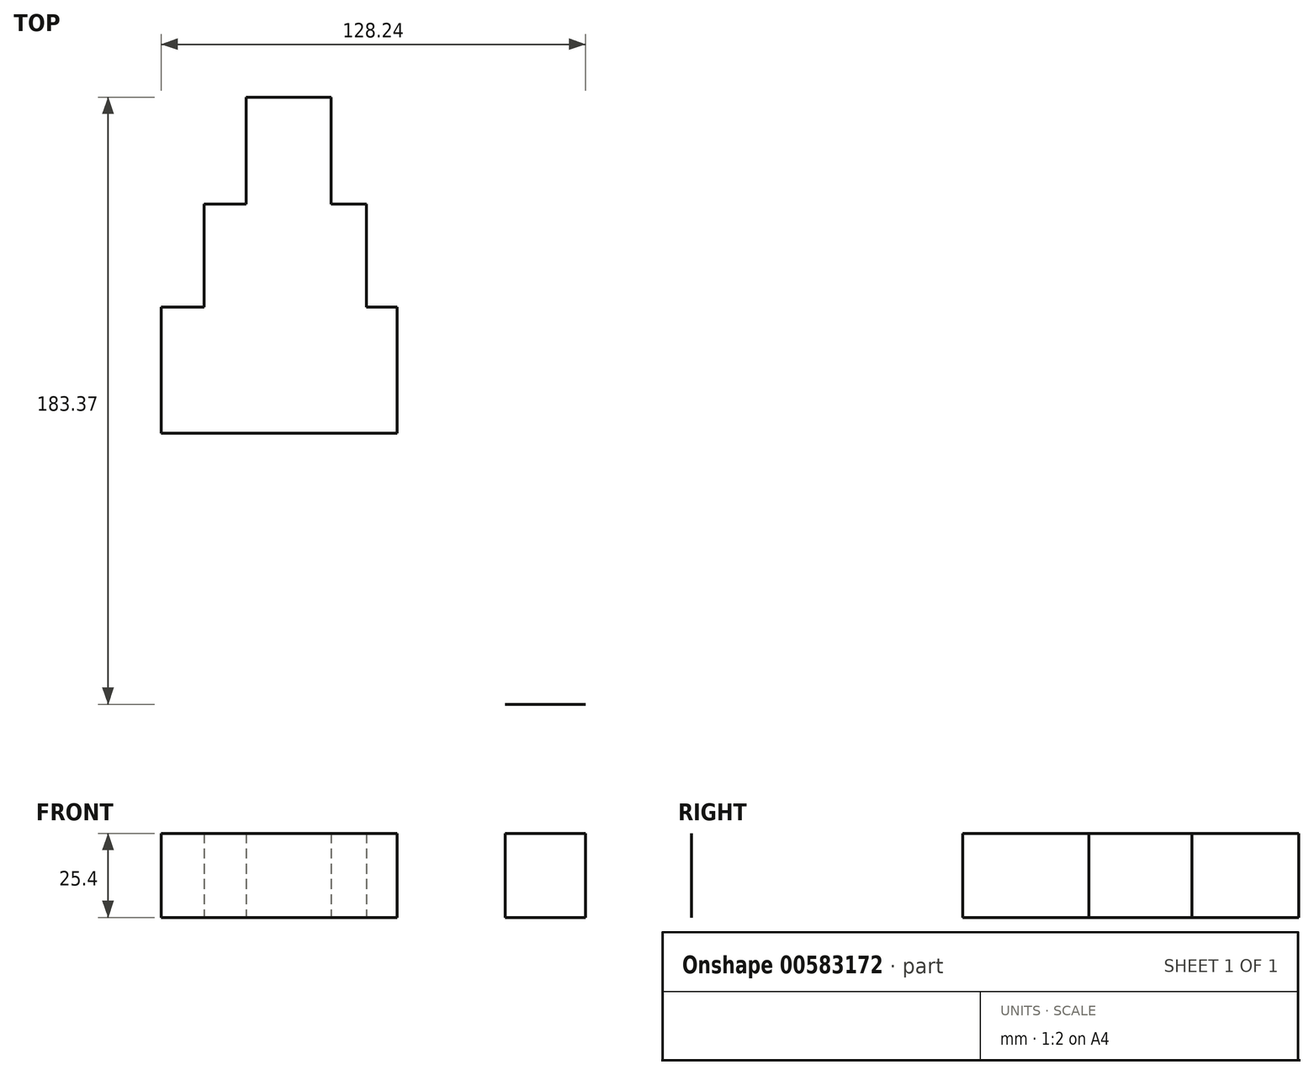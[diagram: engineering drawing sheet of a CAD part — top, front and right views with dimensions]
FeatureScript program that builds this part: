
annotation { "Feature Type Name" : "Feature", "Feature Type Description" : "" }
export const myFeature = defineFeature(function(context is Context, id is Id, definition is map)
    precondition{}
    {
        {
            var Q0;
            Q0=qCreatedBy(makeId("Top.planeOp"),FACE);
            var sketch = newSketch(context, id + "F0", { "sketchPlane" : qUnion([Q0])});
            skLineSegment(sketch, "E0.bottom", {"start": v(-203.2, 189.34) * mm, "end": v(0, 189.34) * mm});
            skLineSegment(sketch, "E0.top", {"start": v(-203.2, -13.86) * mm, "end": v(0, -13.86) * mm});
            skLineSegment(sketch, "E0.left", {"start": v(-203.2, 189.34) * mm, "end": v(-203.2, -13.86) * mm});
            skLineSegment(sketch, "E0.right", {"start": v(0, 189.34) * mm, "end": v(0, -13.86) * mm});
            skText(sketch, "E1", { "text": "A\n", "fontName": "OpenSans-Regular.ttf"});
            skLineSegment(sketch, "E2.bottom", {"start": v(-152.85, 67.96) * mm, "end": v(-81.5, 67.96) * mm});
            skLineSegment(sketch, "E2.top", {"start": v(-152.85, 106.14) * mm, "end": v(-81.5, 106.14) * mm});
            skLineSegment(sketch, "E2.left", {"start": v(-152.85, 67.96) * mm, "end": v(-152.85, 106.14) * mm});
            skLineSegment(sketch, "E2.right", {"start": v(-81.5, 67.96) * mm, "end": v(-81.5, 106.14) * mm});
            skLineSegment(sketch, "E3.bottom", {"start": v(-139.84, 106.14) * mm, "end": v(-90.79, 106.14) * mm});
            skLineSegment(sketch, "E3.top", {"start": v(-139.84, 137.26) * mm, "end": v(-90.79, 137.26) * mm});
            skLineSegment(sketch, "E3.left", {"start": v(-139.84, 106.14) * mm, "end": v(-139.84, 137.26) * mm});
            skLineSegment(sketch, "E3.right", {"start": v(-90.79, 106.14) * mm, "end": v(-90.79, 137.26) * mm});
            skLineSegment(sketch, "E4.bottom", {"start": v(-127.18, 169.5) * mm, "end": v(-101.47, 169.5) * mm});
            skLineSegment(sketch, "E4.top", {"start": v(-127.18, 137.26) * mm, "end": v(-101.47, 137.26) * mm});
            skLineSegment(sketch, "E4.left", {"start": v(-127.18, 169.5) * mm, "end": v(-127.18, 137.26) * mm});
            skLineSegment(sketch, "E4.right", {"start": v(-101.47, 169.5) * mm, "end": v(-101.47, 137.26) * mm});
            const initialGuessF0  = {"E1": [-0.2032, -0.01386, 1, 0, 0.2032]};
            skSetInitialGuess(sketch, initialGuessF0);
            skSolve(sketch);
        }
        {
            var Q0;
            Q0=makeQuery(id+"F0.imprint","IMPRINT",FACE,{"disambiguationData":[TD([[makeQuery(id+"F0.imprint","IMPRINT",EDGE,{"derivedFrom":sQuery(id+"F0.wireOp",EDGE,"E1.sketch_text.stroke-0")}),-1.0]])]});
            extrude(context, id + "F1", {"entities" : qUnion([Q0]), "depth" : 25.4 * mm, "offsetDistance" : 25.4 * mm});
        }
        {
            var Q0;
            {var subQ3=sQuery(id+"F0.wireOp",EDGE,"E2.right");var subQ7=sQuery(id+"F0.wireOp",EDGE,"E1.sketch_text.stroke-8");var subQ9=makeQuery(id+"F0.imprint","INTERSECT",VERTEX,{"derivedFrom":[subQ7,subQ3]});Q0=makeQuery(id+"F0.imprint","IMPRINT",FACE,{"disambiguationData":[TD([[makeQuery(id+"F0.imprint","IMPRINT",EDGE,{"disambiguationData":[TD([[subQ9,-1.0]])],"derivedFrom":subQ7}),1.0]])]});}
            var Q1;
            {var subQ5=sQuery(id+"F0.wireOp",EDGE,"E1.sketch_text.stroke-9");var subQ6=sQuery(id+"F0.wireOp",EDGE,"E1.sketch_text.stroke-8");var subQ7=makeQuery(id+"F0.imprint","INTERSECT",VERTEX,{"derivedFrom":[subQ6,subQ5]});Q1=makeQuery(id+"F0.imprint","IMPRINT",FACE,{"disambiguationData":[TD([[makeQuery(id+"F0.imprint","IMPRINT",EDGE,{"disambiguationData":[TD([[subQ7,1.0]])],"derivedFrom":subQ6}),1.0]])]});}
            var Q2;
            Q2=makeQuery(id+"F0.imprint","IMPRINT",FACE,{"disambiguationData":[TD([[makeQuery(id+"F0.imprint","IMPRINT",EDGE,{"derivedFrom":sQuery(id+"F0.wireOp",EDGE,"E4.bottom")}),-1.0]])]});
            var Q3;
            {var subQ0=sQuery(id+"F0.wireOp",EDGE,"E3.left");Q3=makeQuery(id+"F0.imprint","IMPRINT",FACE,{"disambiguationData":[TD([[makeQuery(id+"F0.imprint","IMPRINT",EDGE,{"derivedFrom":subQ0}),-1.0]])]});}
            var Q4;
            {var subQ4=sQuery(id+"F0.wireOp",EDGE,"E2.bottom");Q4=makeQuery(id+"F0.imprint","IMPRINT",FACE,{"disambiguationData":[TD([[makeQuery(id+"F0.imprint","IMPRINT",EDGE,{"derivedFrom":subQ4}),1.0]])]});}
            var Q5;
            {var subQ0=sQuery(id+"F0.wireOp",EDGE,"E3.right");Q5=makeQuery(id+"F0.imprint","IMPRINT",FACE,{"disambiguationData":[TD([[makeQuery(id+"F0.imprint","IMPRINT",EDGE,{"derivedFrom":subQ0}),1.0]])]});}
            var Q6;
            {var subQ0=sQuery(id+"F0.wireOp",EDGE,"E2.right");var subQ1=sQuery(id+"F0.wireOp",EDGE,"E1.sketch_text.stroke-8");var subQ2=makeQuery(id+"F0.imprint","INTERSECT",VERTEX,{"derivedFrom":[subQ1,subQ0]});Q6=makeQuery(id+"F0.imprint","IMPRINT",FACE,{"disambiguationData":[TD([[makeQuery(id+"F0.imprint","IMPRINT",EDGE,{"disambiguationData":[TD([[subQ2,-1.0]])],"derivedFrom":subQ1}),-1.0]])]});}
            var Q7;
            {var subQ0=sQuery(id+"F0.wireOp",EDGE,"E1.sketch_text.stroke-10");var subQ1=sQuery(id+"F0.wireOp",EDGE,"E1.sketch_text.stroke-9");var subQ2=makeQuery(id+"F0.imprint","INTERSECT",VERTEX,{"derivedFrom":[subQ1,subQ0]});Q7=makeQuery(id+"F0.imprint","IMPRINT",FACE,{"disambiguationData":[TD([[makeQuery(id+"F0.imprint","IMPRINT",EDGE,{"disambiguationData":[TD([[subQ2,1.0]])],"derivedFrom":subQ1}),1.0]])]});}
            extrude(context, id + "F2", {"entities" : qUnion([Q0, Q1, Q2, Q3, Q4, Q5, Q6, Q7]), "operationType" : NewBodyOperationType.ADD, "depth" : 25.4 * mm, "offsetDistance" : 25.4 * mm});
        }
    });
